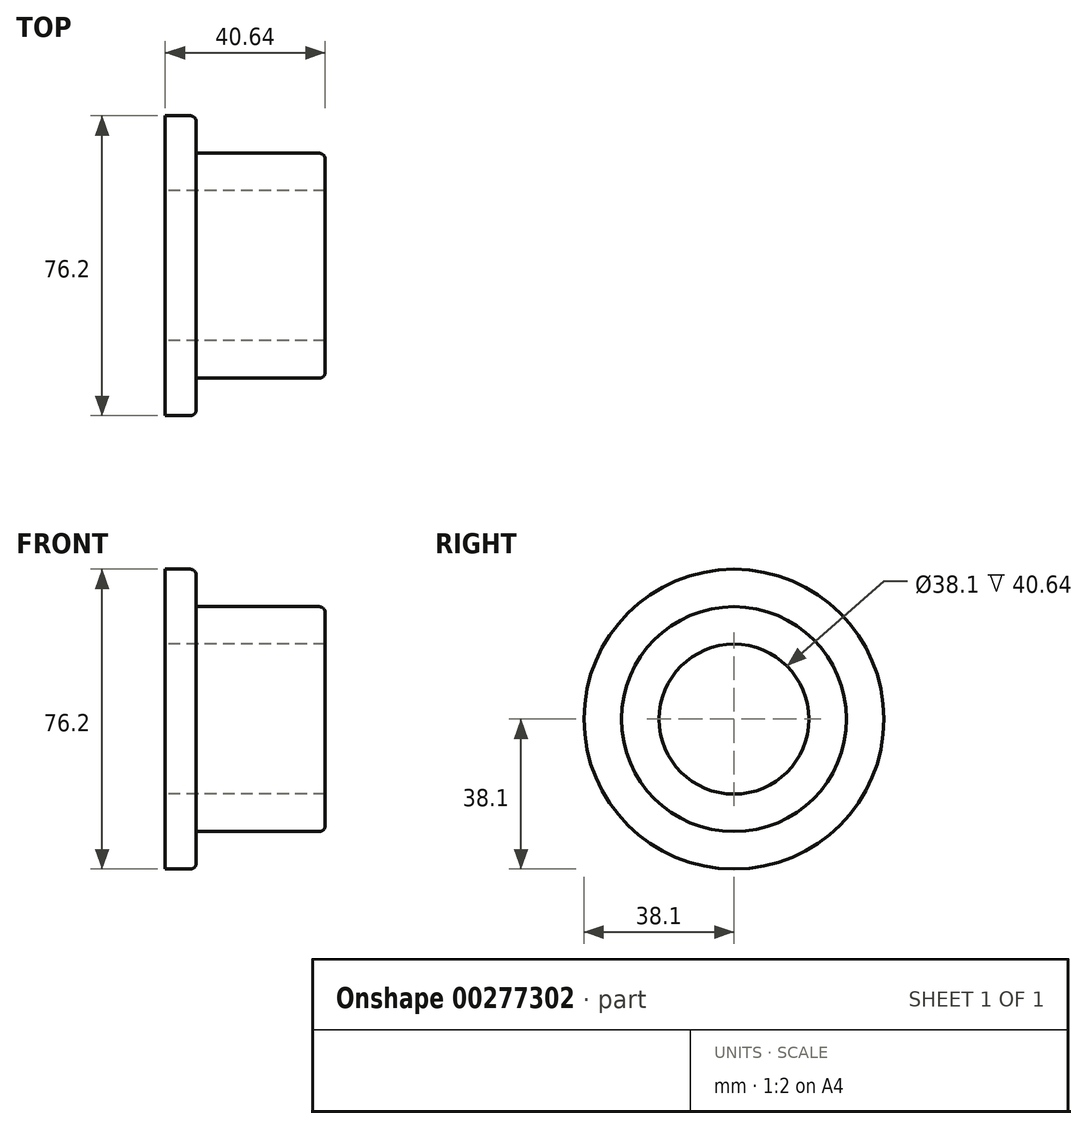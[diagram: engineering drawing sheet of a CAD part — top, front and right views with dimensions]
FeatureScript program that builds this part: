
annotation { "Feature Type Name" : "Feature", "Feature Type Description" : "" }
export const myFeature = defineFeature(function(context is Context, id is Id, definition is map)
    precondition{}
    {
        {
            var Q0;
            Q0=qCreatedBy(makeId("Right.planeOp"),FACE);
            var sketch = newSketch(context, id + "F0", { "sketchPlane" : qUnion([Q0])});
            skCircle(sketch, "E0", {"center": v(0, 0) * mm, "radius": 19.05 * mm});
            skCircle(sketch, "E1", {"center": v(0, 0) * mm, "radius": 38.1 * mm});
            skSolve(sketch);
        }
        {
            var Q0;
            Q0 = qSketchRegion(id + "F0", true);
            extrude(context, id + "F1", {"entities" : qUnion([Q0]), "depth" : 7.87 * mm});
        }
        {
            var Q0;
            Q0=makeQuery(id+"F1.opExtrude","CAP_FACE",FACE,{"disambiguationData":[OSD([sQuery(id+"F0.wireOp",EDGE,"E0"),sQuery(id+"F0.wireOp",EDGE,"E1")])],"isStart":false});
            var sketch = newSketch(context, id + "F2", { "sketchPlane" : qUnion([Q0])});
            skCircle(sketch, "E2.0", {"center": v(0, 0) * mm, "radius": 19.05 * mm});
            skCircle(sketch, "E3", {"center": v(0, 0) * mm, "radius": 28.58 * mm});
            skSolve(sketch);
        }
        {
            var Q0;
            Q0 = qSketchRegion(id + "F2", true);
            extrude(context, id + "F3", {"entities" : qUnion([Q0]), "operationType" : NewBodyOperationType.ADD, "depth" : 32.77 * mm});
        }
        {
            var Q0;
            Q0=makeQuery(id+"F1.opExtrude","CAP_EDGE",EDGE,{"disambiguationData":[OSD([sQuery(id+"F0.wireOp",EDGE,"E1")])],"isStart":false});
            var Q1;
            Q1=makeQuery(id+"F3.opExtrude","CAP_EDGE",EDGE,{"disambiguationData":[OSD([sQuery(id+"F2.wireOp",EDGE,"E3")])],"isStart":true});
            var Q2;
            Q2=makeQuery(id+"F3.opExtrude","CAP_EDGE",EDGE,{"disambiguationData":[OSD([sQuery(id+"F2.wireOp",EDGE,"E3")])],"isStart":false});
            fillet(context, id + "F4", {"entities" : qUnion([Q0, Q1, Q2]), "radius" : 1.52 * mm, "tangentPropagation" : true, "allowEdgeOverflow" : false});
        }
    });
